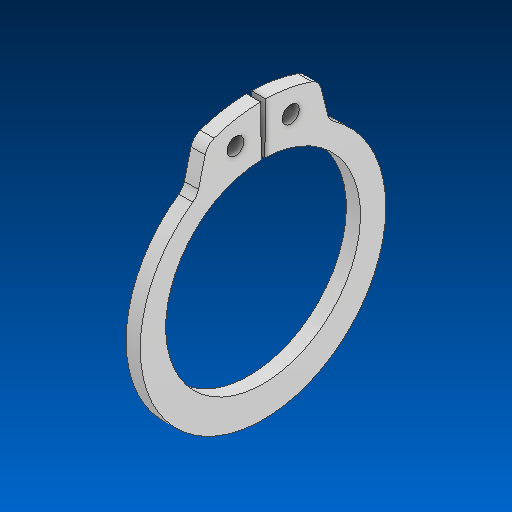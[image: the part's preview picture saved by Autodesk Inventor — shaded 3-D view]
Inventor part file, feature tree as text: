
AUTODESK INVENTOR PART (.ipt)
format: ipt  version: 2022.2 (Build 262287000, 287)  size: 115,200 bytes
history: native  units: in
note: dims shown in document units (in); Inventor stores cm internally (conversion verified against a paired STEP export)
features: fillet x1
ambient origin geometry x8: Origin, YZ Plane, XZ Plane, XY Plane, X Axis, Y Axis, Z Axis, Center Point
bodies: Solid1 (feature_tree)
feature tree (1):
  fillet  "Fillet1"  [1 undecoded]
note: 1 required parameter value undecoded (feature->parameter linkage not recoverable at this tier; creation-order binding heuristic only, values carry confidence <= 0.55)
